# Revit family: 02-60-0035 DN450-500 Reduced Bore
name_source: partatom
category: Pipe Accessories
units: mm (PartAtom-declared; Revit-internal decimal feet)

## family parameters
Always vertical = Yes
Cut with Voids When Loaded = No
Part Type = Valve - Breaks Into
Round Connector Dimension = Use Diameter
Shared = No
Work Plane-Based = No

## types (4) — shared parameters
1 = 1 mm  [stored 0.00328084 ft]
5 = 5 mm  [stored 0.0164042 ft]
Body_Arc = 1200 mm
Body_FL_rib_dim = 928 mm
Body_H = 500 mm
Body_T = 14 mm  [stored 0.0459318 ft]
Bonnet_dim1 = 84 mm  [stored 0.275591 ft]
Bonnet_dim3 = 50 mm  [stored 0.164042 ft]
DN450_PN10 = 02-450-60-006
DN450_PN16 = 02-450-60-016
DN500_PN10 = 02-500-60-006
DN500_PN16 = 02-500-60-016
Description_ = AVK GATE VALVE, FLANGED, PN10-16
F = 16 mm  [stored 0.0524934 ft]
F1 = 20 mm  [stored 0.0656168 ft]
F2 = 55 mm  [stored 0.180446 ft]
H = 958 mm
RIB_T = 8 mm  [stored 0.0262467 ft]
Raised_dis = 4 mm  [stored 0.0131234 ft]
Rib1_H = 150 mm  [stored 0.492126 ft]
Rib1_R = 30 mm  [stored 0.0984252 ft]
Rib1_T = 11 mm  [stored 0.0360892 ft]
Search_table = 02-60-0035 DN450-500 Reduced Bore
Stem = 22 mm  [stored 0.0721785 ft]
Sweep _cut = 5 mm  [stored 0.0164042 ft]
URL_product_pages = https://www.avkvalves.com
logo_H = 250 mm
stem1 = 27 mm  [stored 0.0885827 ft]
zero-valued in all types: Default Elevation

## per-type parameters (varying)
- DN450_PN10: Body_FL_L=325 mm; Body_FL_R=55 mm  [stored 0.180446 ft]; Body_FL_T=30 mm  [stored 0.0984252 ft]; Body_FL_W=135 mm  [stored 0.442913 ft]; Body_FL_arc=1300 mm; Body_FL_rib_dim1=295 mm; Body_L=300 mm; Body_R=35 mm  [stored 0.114829 ft]; Body_W=117 mm  [stored 0.383858 ft]; Body_bottom=270 mm; Bonnet_L=270 mm; Bonnet_d1=94 mm; Bonnet_d2=59 mm; Bonnet_dim2=94 mm; Bore_R=225 mm  [stored 0.738189 ft]; DN=450 mm; Dh=585 mm; Ds=31 mm  [stored 0.101706 ft]; FL_R=320 mm; FL_T=30 mm  [stored 0.0984252 ft]; H3=1278 mm; H3-H=320 mm; L=650 mm; RIB_L=319 mm; RIB_L1=208 mm; Raised_R=260 mm; Rib1_L=320 mm; Rib1_W=140 mm; Rib2_L=320 mm; Rib2_W=140 mm; Rib3_L=320 mm; Rib3_W=140 mm; Rib_T=26 mm; W=320 mm; Wedge_L=99 mm; disk_T=211 mm
- DN450_PN16: Body_FL_L=325 mm; Body_FL_R=55 mm  [stored 0.180446 ft]; Body_FL_T=30 mm  [stored 0.0984252 ft]; Body_FL_W=135 mm  [stored 0.442913 ft]; Body_FL_arc=1300 mm; Body_FL_rib_dim1=295 mm; Body_L=300 mm; Body_R=35 mm  [stored 0.114829 ft]; Body_W=117 mm  [stored 0.383858 ft]; Body_bottom=270 mm; Bonnet_L=270 mm; Bonnet_d1=94 mm; Bonnet_d2=59 mm; Bonnet_dim2=94 mm; Bore_R=225 mm  [stored 0.738189 ft]; DN=450 mm; Dh=585 mm; Ds=31 mm  [stored 0.101706 ft]; FL_R=320 mm; FL_T=30 mm  [stored 0.0984252 ft]; H3=1278 mm; H3-H=320 mm; L=650 mm; RIB_L=319 mm; RIB_L1=208 mm; Raised_R=260 mm; Rib1_L=320 mm; Rib1_W=140 mm; Rib2_L=320 mm; Rib2_W=140 mm; Rib3_L=320 mm; Rib3_W=140 mm; Rib_T=26 mm; W=320 mm; Wedge_L=99 mm; disk_T=211 mm
- DN500_PN10: Body_FL_L=360 mm; Body_FL_R=60 mm  [stored 0.19685 ft]; Body_FL_T=33 mm; Body_FL_W=145 mm  [stored 0.475722 ft]; Body_FL_arc=1350 mm; Body_FL_rib_dim1=319 mm; Body_L=353 mm; Body_R=50 mm  [stored 0.164042 ft]; Body_W=126 mm  [stored 0.413386 ft]; Body_bottom=323 mm; Bonnet_L=318 mm; Bonnet_d1=101 mm; Bonnet_d2=63 mm  [stored 0.206693 ft]; Bonnet_dim2=101 mm; Bore_R=250 mm; DN=500 mm; Dh=650 mm; Ds=34 mm  [stored 0.111549 ft]; FL_R=353 mm; FL_T=32 mm  [stored 0.104987 ft]; H3=1316 mm; H3-H=358 mm; L=700 mm; RIB_L=357 mm; RIB_L1=232 mm; Raised_R=290 mm; Rib1_L=358 mm; Rib1_W=151 mm; Rib2_L=358 mm; Rib2_W=151 mm; Rib3_L=358 mm; Rib3_W=151 mm; Rib_T=28 mm  [stored 0.0918635 ft]; W=358 mm; Wedge_L=107 mm; disk_T=227 mm
- DN500_PN16: Body_FL_L=360 mm; Body_FL_R=60 mm  [stored 0.19685 ft]; Body_FL_T=33 mm; Body_FL_W=145 mm  [stored 0.475722 ft]; Body_FL_arc=1350 mm; Body_FL_rib_dim1=319 mm; Body_L=353 mm; Body_R=50 mm  [stored 0.164042 ft]; Body_W=126 mm  [stored 0.413386 ft]; Body_bottom=323 mm; Bonnet_L=318 mm; Bonnet_d1=101 mm; Bonnet_d2=63 mm  [stored 0.206693 ft]; Bonnet_dim2=101 mm; Bore_R=250 mm; DN=500 mm; Dh=650 mm; Ds=34 mm  [stored 0.111549 ft]; FL_R=353 mm; FL_T=32 mm  [stored 0.104987 ft]; H3=1316 mm; H3-H=358 mm; L=700 mm; RIB_L=357 mm; RIB_L1=232 mm; Raised_R=290 mm; Rib1_L=358 mm; Rib1_W=151 mm; Rib2_L=358 mm; Rib2_W=151 mm; Rib3_L=358 mm; Rib3_W=151 mm; Rib_T=28 mm  [stored 0.0918635 ft]; W=358 mm; Wedge_L=107 mm; disk_T=227 mm

note: [stored X ft] marks values corroborated as IEEE doubles in the binary element streams (Revit-internal decimal feet)

## geometry (parser evidence)
native form markers: Sweep x5
no freeform markers — native parametric forms only
